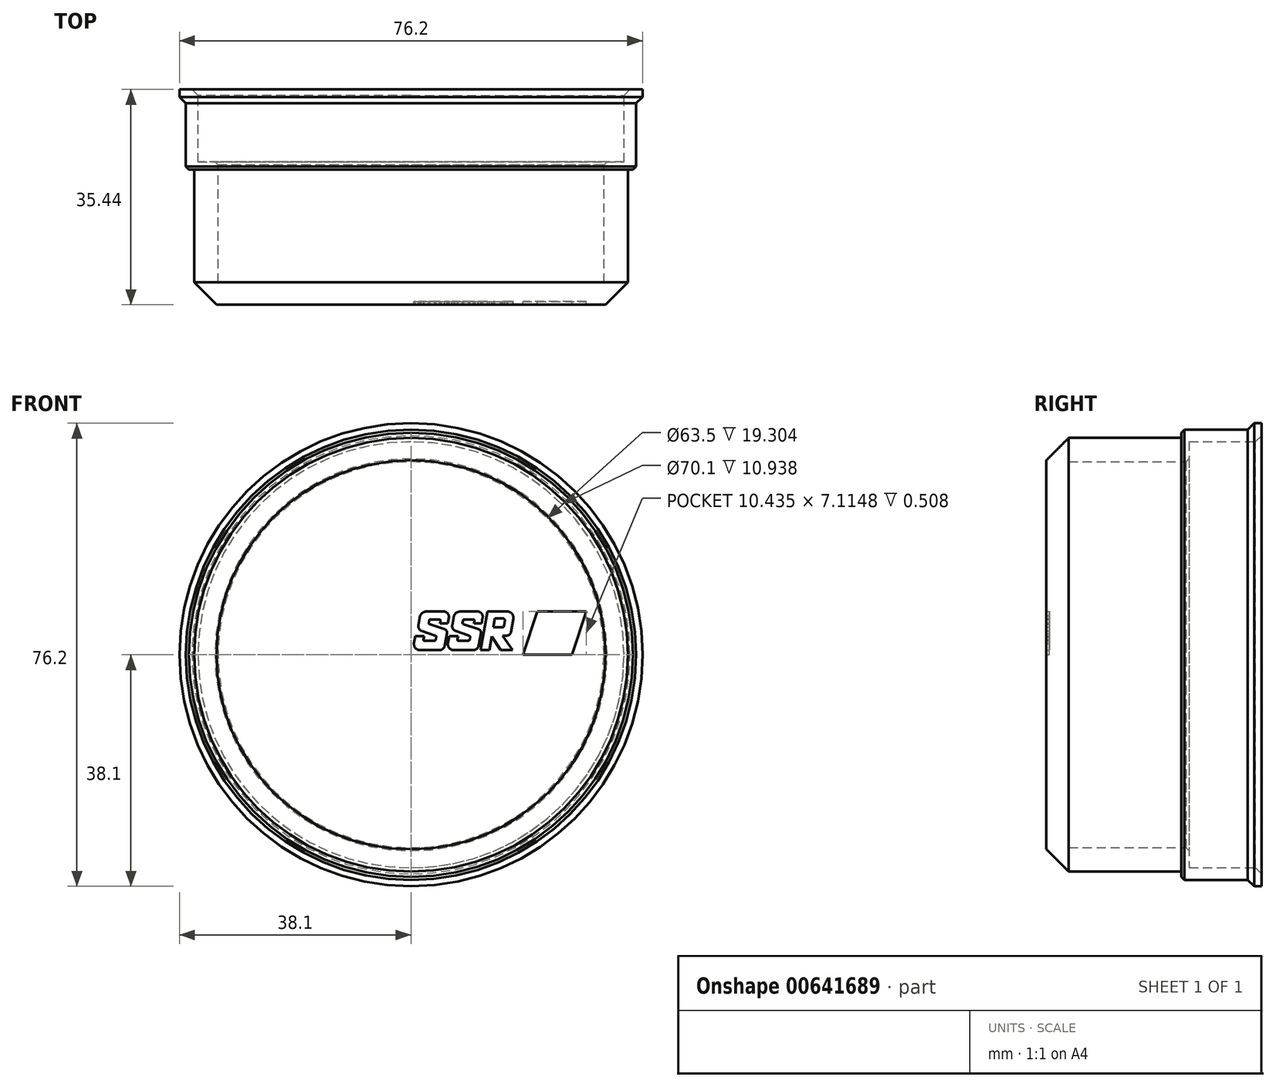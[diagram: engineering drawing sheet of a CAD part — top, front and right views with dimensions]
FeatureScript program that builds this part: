
annotation { "Feature Type Name" : "Feature", "Feature Type Description" : "" }
export const myFeature = defineFeature(function(context is Context, id is Id, definition is map)
    precondition{}
    {
        {
            var Q0;
            Q0=qCreatedBy(makeId("Right.planeOp"),FACE);
            var sketch = newSketch(context, id + "F0", { "sketchPlane" : qUnion([Q0])});
            skLineSegment(sketch, "E0", {"start": v(0, 0) * mm, "end": v(0, 35.69) * mm});
            skLineSegment(sketch, "E1", {"start": v(0, 35.69) * mm, "end": v(21.72, 35.69) * mm});
            skLineSegment(sketch, "E2", {"start": v(21.72, 35.69) * mm, "end": v(21.72, 37.05) * mm});
            skLineSegment(sketch, "E3", {"start": v(21.72, 37.05) * mm, "end": v(32.64, 37.05) * mm});
            skLineSegment(sketch, "E4", {"start": v(3.18, 0) * mm, "end": v(0, 0) * mm});
            skLineSegment(sketch, "E5", {"start": v(22.99, 31.75) * mm, "end": v(22.99, 35.05) * mm});
            skLineSegment(sketch, "E6", {"start": v(22.99, 35.05) * mm, "end": v(34.93, 35.05) * mm});
            skLineSegment(sketch, "E7", {"start": v(32.64, 37.05) * mm, "end": v(33.7, 38.1) * mm});
            skLineSegment(sketch, "E8", {"start": v(34.93, 38.1) * mm, "end": v(34.93, 35.05) * mm});
            skLineSegment(sketch, "E9", {"start": v(3.18, 0) * mm, "end": v(3.18, 31.75) * mm});
            skLineSegment(sketch, "E10", {"start": v(3.18, 31.75) * mm, "end": v(22.99, 31.75) * mm});
            skLineSegment(sketch, "E11", {"start": v(34.93, 38.1) * mm, "end": v(33.7, 38.1) * mm});
            skSolve(sketch);
        }
        {
            var Q0;
            Q0 = qSketchRegion(id + "F0", true);
            var Q1;
            Q1=sQuery(id+"F0.wireOp",EDGE,"E4");
            revolve(context, id + "F1", {"entities" : qUnion([Q0]), "axis" : qUnion([Q1]), "revolveType" : RevolveType.FULL});
        }
        {
            var Q0;
            Q0=makeQuery(id+"F1.opRevolve","SWEPT_EDGE",EDGE,{"disambiguationData":[OSD([sQuery(id+"F0.wireOp",EDGE,"E2"),sQuery(id+"F0.wireOp",EDGE,"E3")])]});
            var Q1;
            Q1=makeQuery(id+"F1.opRevolve","SWEPT_EDGE",EDGE,{"disambiguationData":[OSD([sQuery(id+"F0.wireOp",EDGE,"E5"),sQuery(id+"F0.wireOp",EDGE,"E10")])]});
            chamfer(context, id + "F2", {"entities" : qUnion([Q0, Q1]), "width" : 0.5 * mm, "tangentPropagation" : true});
        }
        {
            var Q0;
            Q0=makeQuery(id+"F1.opRevolve","SWEPT_EDGE",EDGE,{"disambiguationData":[OSD([sQuery(id+"F0.wireOp",EDGE,"E0"),sQuery(id+"F0.wireOp",EDGE,"E1")])]});
            chamfer(context, id + "F3", {"entities" : qUnion([Q0]), "width" : 3.17 * mm, "tangentPropagation" : true});
        }
        {
            var Q0;
            Q0=makeQuery(id+"F1.opRevolve","SWEPT_FACE",FACE,{"disambiguationData":[OSD([sQuery(id+"F0.wireOp",EDGE,"E0")])]});
            var sketch = newSketch(context, id + "F4", { "sketchPlane" : qUnion([Q0])});
            skLineSegment(sketch, "E12", {"start": v(2.49, 7.11) * mm, "end": v(5.51, 7.11) * mm});
            skLineSegment(sketch, "E13", {"start": v(28.84, 7.11) * mm, "end": v(26.5, 0) * mm});
            skLineSegment(sketch, "E14", {"start": v(26.5, 0) * mm, "end": v(18.4, 0) * mm});
            skLineSegment(sketch, "E15", {"start": v(18.4, 0) * mm, "end": v(20.76, 7.11) * mm});
            skLineSegment(sketch, "E16", {"start": v(23.46, 7.11) * mm, "end": v(21.11, 0) * mm});
            skLineSegment(sketch, "E17", {"start": v(23.8, 0) * mm, "end": v(26.16, 7.11) * mm});
            skLineSegment(sketch, "E18", {"start": v(4.79, 5.2) * mm, "end": v(6.05, 5.2) * mm});
            skLineSegment(sketch, "E19", {"start": v(0.73, 3.08) * mm, "end": v(2.17, 3.08) * mm});
            skLineSegment(sketch, "E20", {"start": v(1.2, 0.8) * mm, "end": v(4.97, 0.8) * mm});
            skLineSegment(sketch, "E21", {"start": v(16.7, 0.8) * mm, "end": v(14.78, 0.8) * mm});
            skLineSegment(sketch, "E22", {"start": v(12.9, 0.8) * mm, "end": v(13.31, 3.03) * mm});
            skLineSegment(sketch, "E23", {"start": v(13.31, 3.03) * mm, "end": v(14.78, 0.8) * mm});
            skLineSegment(sketch, "E24", {"start": v(15.08, 3.16) * mm, "end": v(16.7, 0.8) * mm});
            skLineSegment(sketch, "E25", {"start": v(12.57, 7.11) * mm, "end": v(11.42, 0.8) * mm});
            skLineSegment(sketch, "E26", {"start": v(13.83, 5.97) * mm, "end": v(13.57, 4.5) * mm});
            skLineSegment(sketch, "E27", {"start": v(13.57, 4.5) * mm, "end": v(14.97, 4.5) * mm});
            skLineSegment(sketch, "E28", {"start": v(13.83, 5.97) * mm, "end": v(15.15, 5.97) * mm});
            skLineSegment(sketch, "E29", {"start": v(15.45, 5.62) * mm, "end": v(15.3, 4.77) * mm});
            skLineSegment(sketch, "E30", {"start": v(15.08, 3.16) * mm, "end": v(15.82, 3.16) * mm});
            skLineSegment(sketch, "E31", {"start": v(16.85, 5.93) * mm, "end": v(16.46, 3.75) * mm});
            skLineSegment(sketch, "E32", {"start": v(2.16, 2.33) * mm, "end": v(3.91, 2.33) * mm});
            skLineSegment(sketch, "E33", {"start": v(2.17, 3.08) * mm, "end": v(2.06, 2.5) * mm});
            skLineSegment(sketch, "E34", {"start": v(0.73, 3.08) * mm, "end": v(0.49, 1.84) * mm});
            skArc(sketch, "E35", {"start": v(14.97, 4.5) * mm, "mid": v(15.19, 4.57) * mm, "end": v(15.3, 4.77) * mm});
            skArc(sketch, "E36", {"start": v(15.45, 5.62) * mm, "mid": v(15.38, 5.86) * mm, "end": v(15.15, 5.97) * mm});
            skArc(sketch, "E37", {"start": v(16.85, 5.93) * mm, "mid": v(16.66, 6.72) * mm, "end": v(15.96, 7.11) * mm});
            skArc(sketch, "E38", {"start": v(15.82, 3.16) * mm, "mid": v(16.24, 3.35) * mm, "end": v(16.46, 3.75) * mm});
            skLineSegment(sketch, "E39.trimOffspring", {"start": v(14.78, 0.8) * mm, "end": v(16.7, 0.8) * mm});
            skLineSegment(sketch, "E40", {"start": v(5.56, 1.51) * mm, "end": v(5.93, 3.49) * mm});
            skLineSegment(sketch, "E41", {"start": v(3.04, 5.07) * mm, "end": v(5.55, 4.2) * mm});
            skLineSegment(sketch, "E42", {"start": v(4.1, 2.52) * mm, "end": v(4.17, 2.9) * mm});
            skLineSegment(sketch, "E43", {"start": v(1.66, 3.97) * mm, "end": v(4, 3.14) * mm});
            skLineSegment(sketch, "E44", {"start": v(1.5, 6.44) * mm, "end": v(1.21, 4.85) * mm});
            skLineSegment(sketch, "E45", {"start": v(3, 5.68) * mm, "end": v(2.92, 5.24) * mm});
            skLineSegment(sketch, "E46", {"start": v(4.79, 5.2) * mm, "end": v(4.87, 5.6) * mm});
            skLineSegment(sketch, "E47", {"start": v(6.05, 5.2) * mm, "end": v(6.22, 6.1) * mm});
            skArc(sketch, "E48", {"start": v(4.87, 5.6) * mm, "mid": v(4.84, 5.74) * mm, "end": v(4.71, 5.82) * mm});
            skArc(sketch, "E49", {"start": v(6.22, 6.1) * mm, "mid": v(6.08, 6.76) * mm, "end": v(5.51, 7.11) * mm});
            skArc(sketch, "E50", {"start": v(3.13, 5.82) * mm, "mid": v(3.05, 5.77) * mm, "end": v(3, 5.68) * mm});
            skArc(sketch, "E51", {"start": v(2.49, 7.11) * mm, "mid": v(1.9, 6.93) * mm, "end": v(1.5, 6.44) * mm});
            skArc(sketch, "E52", {"start": v(2.92, 5.24) * mm, "mid": v(2.94, 5.13) * mm, "end": v(3.04, 5.07) * mm});
            skArc(sketch, "E53", {"start": v(1.21, 4.85) * mm, "mid": v(1.29, 4.33) * mm, "end": v(1.66, 3.97) * mm});
            skArc(sketch, "E54", {"start": v(5.93, 3.49) * mm, "mid": v(5.87, 3.92) * mm, "end": v(5.55, 4.2) * mm});
            skArc(sketch, "E55", {"start": v(4.17, 2.9) * mm, "mid": v(4.12, 3.05) * mm, "end": v(4, 3.14) * mm});
            skArc(sketch, "E56", {"start": v(3.91, 2.33) * mm, "mid": v(4.04, 2.4) * mm, "end": v(4.1, 2.52) * mm});
            skArc(sketch, "E57", {"start": v(2.06, 2.5) * mm, "mid": v(2.06, 2.39) * mm, "end": v(2.16, 2.33) * mm});
            skArc(sketch, "E58", {"start": v(0.49, 1.84) * mm, "mid": v(0.66, 1.2) * mm, "end": v(1.2, 0.8) * mm});
            skArc(sketch, "E59", {"start": v(4.97, 0.8) * mm, "mid": v(5.36, 1.08) * mm, "end": v(5.56, 1.51) * mm});
            skLineSegment(sketch, "E60.trimOffspring", {"start": v(6.3, 3.08) * mm, "end": v(7.75, 3.08) * mm});
            skLineSegment(sketch, "E61.trimOffspring", {"start": v(4.71, 5.82) * mm, "end": v(3.13, 5.82) * mm});
            skLineSegment(sketch, "E62", {"start": v(8.06, 7.11) * mm, "end": v(11.09, 7.11) * mm});
            skLineSegment(sketch, "E63", {"start": v(10.36, 5.2) * mm, "end": v(11.62, 5.2) * mm});
            skLineSegment(sketch, "E64", {"start": v(6.78, 0.8) * mm, "end": v(10.54, 0.8) * mm});
            skLineSegment(sketch, "E65", {"start": v(7.75, 3.08) * mm, "end": v(7.63, 2.5) * mm});
            skLineSegment(sketch, "E66", {"start": v(6.3, 3.08) * mm, "end": v(6.06, 1.84) * mm});
            skLineSegment(sketch, "E67", {"start": v(11.13, 1.51) * mm, "end": v(11.5, 3.49) * mm});
            skLineSegment(sketch, "E68", {"start": v(8.61, 5.07) * mm, "end": v(11.12, 4.2) * mm});
            skLineSegment(sketch, "E69", {"start": v(9.68, 2.52) * mm, "end": v(9.74, 2.9) * mm});
            skLineSegment(sketch, "E70", {"start": v(7.24, 3.97) * mm, "end": v(9.58, 3.14) * mm});
            skLineSegment(sketch, "E71", {"start": v(7.08, 6.44) * mm, "end": v(6.79, 4.85) * mm});
            skLineSegment(sketch, "E72", {"start": v(8.57, 5.68) * mm, "end": v(8.5, 5.24) * mm});
            skLineSegment(sketch, "E73", {"start": v(10.36, 5.2) * mm, "end": v(10.44, 5.6) * mm});
            skLineSegment(sketch, "E74", {"start": v(11.62, 5.2) * mm, "end": v(11.8, 6.1) * mm});
            skArc(sketch, "E75", {"start": v(10.44, 5.6) * mm, "mid": v(10.41, 5.74) * mm, "end": v(10.29, 5.82) * mm});
            skArc(sketch, "E76", {"start": v(11.8, 6.1) * mm, "mid": v(11.65, 6.76) * mm, "end": v(11.09, 7.11) * mm});
            skArc(sketch, "E77", {"start": v(8.7, 5.82) * mm, "mid": v(8.62, 5.77) * mm, "end": v(8.57, 5.68) * mm});
            skArc(sketch, "E78", {"start": v(8.06, 7.11) * mm, "mid": v(7.47, 6.93) * mm, "end": v(7.08, 6.44) * mm});
            skArc(sketch, "E79", {"start": v(8.5, 5.24) * mm, "mid": v(8.52, 5.13) * mm, "end": v(8.61, 5.07) * mm});
            skArc(sketch, "E80", {"start": v(6.79, 4.85) * mm, "mid": v(6.86, 4.33) * mm, "end": v(7.24, 3.97) * mm});
            skArc(sketch, "E81", {"start": v(11.5, 3.49) * mm, "mid": v(11.45, 3.92) * mm, "end": v(11.12, 4.2) * mm});
            skArc(sketch, "E82", {"start": v(9.74, 2.9) * mm, "mid": v(9.7, 3.05) * mm, "end": v(9.58, 3.14) * mm});
            skArc(sketch, "E83", {"start": v(9.49, 2.33) * mm, "mid": v(9.62, 2.4) * mm, "end": v(9.68, 2.52) * mm});
            skArc(sketch, "E84", {"start": v(7.63, 2.5) * mm, "mid": v(7.64, 2.39) * mm, "end": v(7.74, 2.33) * mm});
            skArc(sketch, "E85", {"start": v(6.06, 1.84) * mm, "mid": v(6.23, 1.2) * mm, "end": v(6.78, 0.8) * mm});
            skArc(sketch, "E86", {"start": v(10.54, 0.8) * mm, "mid": v(10.93, 1.08) * mm, "end": v(11.13, 1.51) * mm});
            skLineSegment(sketch, "E87.trimOffspring", {"start": v(10.29, 5.82) * mm, "end": v(8.7, 5.82) * mm});
            skLineSegment(sketch, "E88.trimOffspring", {"start": v(7.74, 2.33) * mm, "end": v(9.49, 2.33) * mm});
            skLineSegment(sketch, "E89.trimOffspring", {"start": v(11.42, 0.8) * mm, "end": v(12.9, 0.8) * mm});
            skLineSegment(sketch, "E90.trimOffspring", {"start": v(20.76, 7.11) * mm, "end": v(28.84, 7.11) * mm});
            skLineSegment(sketch, "E91.trimOffspring", {"start": v(12.57, 7.11) * mm, "end": v(15.96, 7.11) * mm});
            skSolve(sketch);
        }
        {
            var Q0;
            Q0=makeQuery(id+"F4.imprint","IMPRINT",FACE,{"disambiguationData":[TD([[makeQuery(id+"F4.imprint","IMPRINT",EDGE,{"derivedFrom":sQuery(id+"F4.wireOp",EDGE,"E12")}),1.0]])]});
            var Q1;
            Q1=makeQuery(id+"F4.imprint","IMPRINT",FACE,{"disambiguationData":[TD([[makeQuery(id+"F4.imprint","IMPRINT",EDGE,{"derivedFrom":sQuery(id+"F4.wireOp",EDGE,"E26")}),1.0]])]});
            extrude(context, id + "F5", {"entities" : qUnion([Q0, Q1]), "operationType" : NewBodyOperationType.ADD, "depth" : 0.5 * mm, "offsetDistance" : 25.4 * mm});
        }
        {
            var Q0;
            Q0=makeQuery(id+"F5.opExtrude","CAP_EDGE",EDGE,{"disambiguationData":[OSD([sQuery(id+"F0.wireOp",EDGE,"E0"),sQuery(id+"F0.wireOp",EDGE,"E1")])],"isStart":false});
            chamfer(context, id + "F6", {"entities" : qUnion([Q0]), "width" : 0.5 * mm, "tangentPropagation" : true});
        }
        {
            var Q0;
            Q0=makeQuery(id+"F1.opRevolve","SWEPT_EDGE",EDGE,{"disambiguationData":[OSD([sQuery(id+"F0.wireOp",EDGE,"E6"),sQuery(id+"F0.wireOp",EDGE,"E8")])]});
            chamfer(context, id + "F7", {"entities" : qUnion([Q0]), "width" : 1 * mm, "tangentPropagation" : true});
        }
    });
